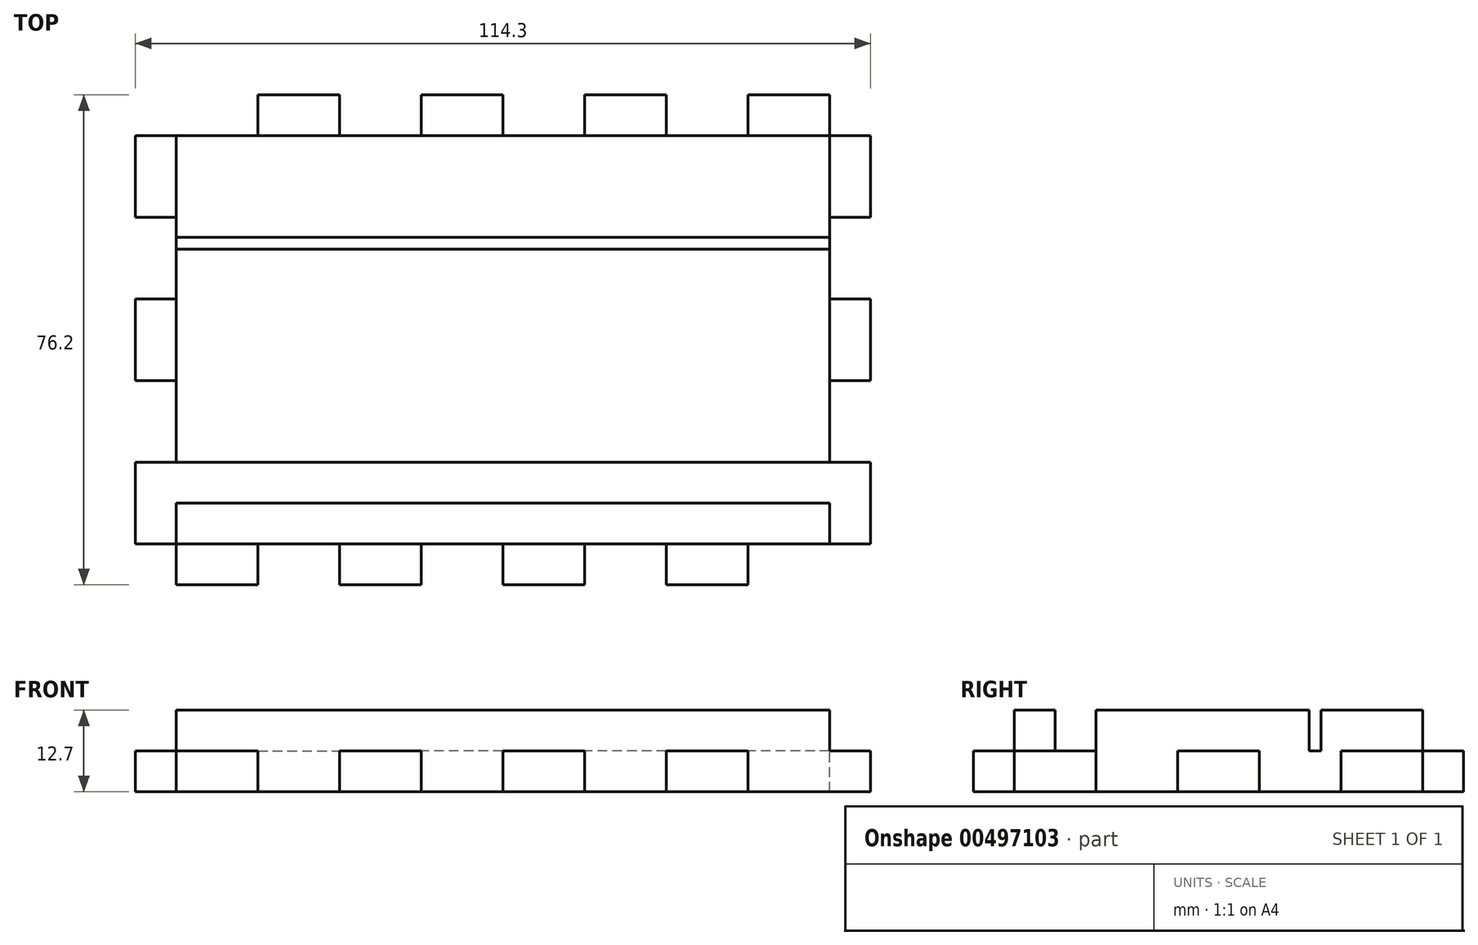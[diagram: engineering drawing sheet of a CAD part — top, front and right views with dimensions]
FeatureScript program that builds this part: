
annotation { "Feature Type Name" : "Feature", "Feature Type Description" : "" }
export const myFeature = defineFeature(function(context is Context, id is Id, definition is map)
    precondition{}
    {
        {
            var Q0;
            Q0=qCreatedBy(makeId("Top.planeOp"),FACE);
            var sketch = newSketch(context, id + "F0", { "sketchPlane" : qUnion([Q0])});
            skLineSegment(sketch, "E0.bottom", {"start": v(50.8, 31.75) * mm, "end": v(-50.8, 31.75) * mm});
            skLineSegment(sketch, "E0.top", {"start": v(50.8, -31.75) * mm, "end": v(-50.8, -31.75) * mm});
            skLineSegment(sketch, "E0.left", {"start": v(50.8, 31.75) * mm, "end": v(50.8, -31.75) * mm});
            skLineSegment(sketch, "E0.right", {"start": v(-50.8, 31.75) * mm, "end": v(-50.8, -31.75) * mm});
            skPoint(sketch, "E0.middle", {"position": v(0, 0) * mm});
            skSolve(sketch);
        }
        {
            var Q0;
            Q0=makeQuery(id+"F0.imprint","IMPRINT",FACE,{"disambiguationData":[TD([[makeQuery(id+"F0.imprint","IMPRINT",EDGE,{"derivedFrom":sQuery(id+"F0.wireOp",EDGE,"E0.bottom")}),1.0]])]});
            extrude(context, id + "F1", {"entities" : qUnion([Q0]), "depth" : 6.35 * mm});
        }
        {
            var Q0;
            Q0=makeQuery(id+"F1.opExtrude","CAP_FACE",FACE,{"disambiguationData":[OSD([sQuery(id+"F0.wireOp",EDGE,"E0.bottom"),sQuery(id+"F0.wireOp",EDGE,"E0.top"),sQuery(id+"F0.wireOp",EDGE,"E0.left"),sQuery(id+"F0.wireOp",EDGE,"E0.right")])],"isStart":false});
            var sketch = newSketch(context, id + "F2", { "sketchPlane" : qUnion([Q0])});
            skLineSegment(sketch, "E1.bottom", {"start": v(50.8, -31.75) * mm, "end": v(-50.8, -31.75) * mm});
            skLineSegment(sketch, "E1.top", {"start": v(50.8, -25.4) * mm, "end": v(-50.8, -25.4) * mm});
            skLineSegment(sketch, "E1.left", {"start": v(50.8, -31.75) * mm, "end": v(50.8, -25.4) * mm});
            skLineSegment(sketch, "E1.right", {"start": v(-50.8, -31.75) * mm, "end": v(-50.8, -25.4) * mm});
            skSolve(sketch);
        }
        {
            var Q0;
            Q0=makeQuery(id+"F2.imprint","IMPRINT",FACE,{"disambiguationData":[TD([[makeQuery(id+"F2.imprint","IMPRINT",EDGE,{"derivedFrom":sQuery(id+"F2.wireOp",EDGE,"E1.bottom")}),-1.0]])]});
            extrude(context, id + "F3", {"entities" : qUnion([Q0]), "operationType" : NewBodyOperationType.ADD, "depth" : 6.35 * mm});
        }
        {
            var Q0;
            Q0=makeQuery(id+"F1.opExtrude","CAP_FACE",FACE,{"disambiguationData":[OSD([sQuery(id+"F0.wireOp",EDGE,"E0.bottom"),sQuery(id+"F0.wireOp",EDGE,"E0.top"),sQuery(id+"F0.wireOp",EDGE,"E0.left"),sQuery(id+"F0.wireOp",EDGE,"E0.right")])],"isStart":false});
            var sketch = newSketch(context, id + "F4", { "sketchPlane" : qUnion([Q0])});
            skLineSegment(sketch, "E2", {"start": v(50.8, -25.4) * mm, "end": v(50.8, -6.22) * mm});
            skLineSegment(sketch, "E3.bottom", {"start": v(50.8, -6.22) * mm, "end": v(-50.8, -6.22) * mm});
            skLineSegment(sketch, "E3.top", {"start": v(50.8, 14.1) * mm, "end": v(-50.8, 14.1) * mm});
            skLineSegment(sketch, "E3.left", {"start": v(50.8, -6.22) * mm, "end": v(50.8, 14.1) * mm});
            skLineSegment(sketch, "E3.right", {"start": v(-50.8, -6.22) * mm, "end": v(-50.8, 14.1) * mm});
            skSolve(sketch);
        }
        {
            var Q0;
            Q0=makeQuery(id+"F4.imprint","IMPRINT",FACE,{"disambiguationData":[TD([[makeQuery(id+"F4.imprint","IMPRINT",EDGE,{"derivedFrom":sQuery(id+"F4.wireOp",EDGE,"E3.bottom")}),-1.0]])]});
            extrude(context, id + "F5", {"entities" : qUnion([Q0]), "operationType" : NewBodyOperationType.ADD, "depth" : 6.35 * mm});
        }
        {
            var Q0;
            {var subQ0=sQuery(id+"F0.wireOp",EDGE,"E0.right");var subQ1=sQuery(id+"F0.wireOp",EDGE,"E0.left");var subQ2=sQuery(id+"F0.wireOp",EDGE,"E0.bottom");Q0=makeQuery(id+"F5.boolean.opBoolean","SPLIT",FACE,{"disambiguationData":[TD([makeQuery(id+"F1.opExtrude","SWEPT_FACE",FACE,{"disambiguationData":[OSD([subQ2])]})])],"derivedFrom":makeQuery(id+"F1.opExtrude","CAP_FACE",FACE,{"disambiguationData":[OSD([subQ2,sQuery(id+"F0.wireOp",EDGE,"E0.top"),subQ1,subQ0])],"isStart":false})});}
            var sketch = newSketch(context, id + "F6", { "sketchPlane" : qUnion([Q0])});
            skLineSegment(sketch, "E4.bottom", {"start": v(-50.8, 14.1) * mm, "end": v(50.8, 14.1) * mm});
            skLineSegment(sketch, "E4.top", {"start": v(-50.8, 22.92) * mm, "end": v(50.8, 22.92) * mm});
            skLineSegment(sketch, "E4.left", {"start": v(-50.8, 14.1) * mm, "end": v(-50.8, 22.92) * mm});
            skLineSegment(sketch, "E4.right", {"start": v(50.8, 14.1) * mm, "end": v(50.8, 22.92) * mm});
            skSolve(sketch);
        }
        {
            var Q0;
            {var subQ0=sQuery(id+"F6.wireOp",EDGE,"E4.top");Q0=makeQuery(id+"F6.imprint","IMPRINT",FACE,{"disambiguationData":[TD([[makeQuery(id+"F6.imprint","IMPRINT",EDGE,{"derivedFrom":subQ0}),1.0]])]});}
            extrude(context, id + "F7", {"entities" : qUnion([Q0]), "operationType" : NewBodyOperationType.ADD, "depth" : 6.35 * mm});
        }
        {
            var Q0;
            Q0=makeQuery(id+"F3.boolean.opBoolean","MERGE",FACE,{"derivedFrom":[makeQuery(id+"F1.opExtrude","SWEPT_FACE",FACE,{"disambiguationData":[OSD([sQuery(id+"F0.wireOp",EDGE,"E0.top")])]}),makeQuery(id+"F3.opExtrude","SWEPT_FACE",FACE,{"disambiguationData":[OSD([sQuery(id+"F2.wireOp",EDGE,"E1.bottom")])]})]});
            var sketch = newSketch(context, id + "F8", { "sketchPlane" : qUnion([Q0])});
            skLineSegment(sketch, "E5.bottom", {"start": v(-50.8, 0) * mm, "end": v(-38.1, 0) * mm});
            skLineSegment(sketch, "E5.top", {"start": v(-50.8, 6.35) * mm, "end": v(-38.1, 6.35) * mm});
            skLineSegment(sketch, "E5.left", {"start": v(-50.8, 0) * mm, "end": v(-50.8, 6.35) * mm});
            skLineSegment(sketch, "E5.right", {"start": v(-38.1, 0) * mm, "end": v(-38.1, 6.35) * mm});
            skLineSegment(sketch, "E6.bottom", {"start": v(-25.4, 0) * mm, "end": v(-12.7, 0) * mm});
            skLineSegment(sketch, "E6.top", {"start": v(-25.4, 6.35) * mm, "end": v(-12.7, 6.35) * mm});
            skLineSegment(sketch, "E6.left", {"start": v(-25.4, 0) * mm, "end": v(-25.4, 6.35) * mm});
            skLineSegment(sketch, "E6.right", {"start": v(-12.7, 0) * mm, "end": v(-12.7, 6.35) * mm});
            skLineSegment(sketch, "E7", {"start": v(-12.7, 0) * mm, "end": v(0, 0) * mm});
            skLineSegment(sketch, "E8.bottom", {"start": v(0, 0) * mm, "end": v(12.7, 0) * mm});
            skLineSegment(sketch, "E8.top", {"start": v(0, 6.35) * mm, "end": v(12.7, 6.35) * mm});
            skLineSegment(sketch, "E8.left", {"start": v(0, 0) * mm, "end": v(0, 6.35) * mm});
            skLineSegment(sketch, "E8.right", {"start": v(12.7, 0) * mm, "end": v(12.7, 6.35) * mm});
            skLineSegment(sketch, "E9.bottom", {"start": v(25.4, 0) * mm, "end": v(38.1, 0) * mm});
            skLineSegment(sketch, "E9.top", {"start": v(25.4, 6.35) * mm, "end": v(38.1, 6.35) * mm});
            skLineSegment(sketch, "E9.left", {"start": v(25.4, 0) * mm, "end": v(25.4, 6.35) * mm});
            skLineSegment(sketch, "E9.right", {"start": v(38.1, 0) * mm, "end": v(38.1, 6.35) * mm});
            skSolve(sketch);
        }
        {
            var Q0;
            Q0=makeQuery(id+"F8.imprint","IMPRINT",FACE,{"disambiguationData":[TD([[makeQuery(id+"F8.imprint","IMPRINT",EDGE,{"derivedFrom":sQuery(id+"F8.wireOp",EDGE,"E5.bottom")}),-1.0]])]});
            var Q1;
            Q1=makeQuery(id+"F8.imprint","IMPRINT",FACE,{"disambiguationData":[TD([[makeQuery(id+"F8.imprint","IMPRINT",EDGE,{"derivedFrom":sQuery(id+"F8.wireOp",EDGE,"E6.bottom")}),-1.0]])]});
            var Q2;
            Q2=makeQuery(id+"F8.imprint","IMPRINT",FACE,{"disambiguationData":[TD([[makeQuery(id+"F8.imprint","IMPRINT",EDGE,{"derivedFrom":sQuery(id+"F8.wireOp",EDGE,"E8.bottom")}),-1.0]])]});
            var Q3;
            Q3=makeQuery(id+"F8.imprint","IMPRINT",FACE,{"disambiguationData":[TD([[makeQuery(id+"F8.imprint","IMPRINT",EDGE,{"derivedFrom":sQuery(id+"F8.wireOp",EDGE,"E9.bottom")}),-1.0]])]});
            extrude(context, id + "F9", {"entities" : qUnion([Q0, Q1, Q2, Q3]), "operationType" : NewBodyOperationType.ADD, "depth" : 6.35 * mm});
        }
        {
            var Q0;
            {var subQ0=sQuery(id+"F0.wireOp",EDGE,"E0.bottom");Q0=makeQuery(id+"F7.boolean.opBoolean","MERGE",FACE,{"derivedFrom":[makeQuery(id+"F1.opExtrude","SWEPT_FACE",FACE,{"disambiguationData":[OSD([subQ0])]}),makeQuery(id+"F7.opExtrude","SWEPT_FACE",FACE,{"disambiguationData":[OSD([subQ0])]})]});}
            var sketch = newSketch(context, id + "F10", { "sketchPlane" : qUnion([Q0])});
            skLineSegment(sketch, "E10", {"start": v(38.1, 6.35) * mm, "end": v(25.4, 6.35) * mm});
            skLineSegment(sketch, "E11.bottom", {"start": v(-50.8, 0) * mm, "end": v(-38.1, 0) * mm});
            skLineSegment(sketch, "E11.top", {"start": v(-50.8, 6.35) * mm, "end": v(-38.1, 6.35) * mm});
            skLineSegment(sketch, "E11.left", {"start": v(-50.8, 0) * mm, "end": v(-50.8, 6.35) * mm});
            skLineSegment(sketch, "E11.right", {"start": v(-38.1, 0) * mm, "end": v(-38.1, 6.35) * mm});
            skLineSegment(sketch, "E12.bottom", {"start": v(-25.4, 0) * mm, "end": v(-12.7, 0) * mm});
            skLineSegment(sketch, "E12.top", {"start": v(-25.4, 6.35) * mm, "end": v(-12.7, 6.35) * mm});
            skLineSegment(sketch, "E12.left", {"start": v(-25.4, 0) * mm, "end": v(-25.4, 6.35) * mm});
            skLineSegment(sketch, "E12.right", {"start": v(-12.7, 0) * mm, "end": v(-12.7, 6.35) * mm});
            skLineSegment(sketch, "E13.bottom", {"start": v(0, 0) * mm, "end": v(12.7, 0) * mm});
            skLineSegment(sketch, "E13.top", {"start": v(0, 6.35) * mm, "end": v(12.7, 6.35) * mm});
            skLineSegment(sketch, "E13.left", {"start": v(0, 0) * mm, "end": v(0, 6.35) * mm});
            skLineSegment(sketch, "E13.right", {"start": v(12.7, 0) * mm, "end": v(12.7, 6.35) * mm});
            skLineSegment(sketch, "E14.bottom", {"start": v(25.4, 0) * mm, "end": v(38.1, 0) * mm});
            skLineSegment(sketch, "E14.top", {"start": v(25.4, 6.35) * mm, "end": v(38.1, 6.35) * mm});
            skLineSegment(sketch, "E14.left", {"start": v(25.4, 0) * mm, "end": v(25.4, 6.35) * mm});
            skLineSegment(sketch, "E14.right", {"start": v(38.1, 0) * mm, "end": v(38.1, 6.35) * mm});
            skLineSegment(sketch, "E15.trimOffspring", {"start": v(12.7, 6.35) * mm, "end": v(0, 6.35) * mm});
            skPoint(sketch, "E16.orphan", {"position": v(50.8, 6.35) * mm});
            skLineSegment(sketch, "E17.trimOffspring", {"start": v(-12.7, 6.35) * mm, "end": v(-25.4, 6.35) * mm});
            skLineSegment(sketch, "E18.trimOffspring", {"start": v(-38.1, 6.35) * mm, "end": v(-50.8, 6.35) * mm});
            skSolve(sketch);
        }
        {
            var Q0;
            Q0=makeQuery(id+"F10.imprint","IMPRINT",FACE,{"disambiguationData":[TD([[makeQuery(id+"F10.imprint","IMPRINT",EDGE,{"derivedFrom":sQuery(id+"F10.wireOp",EDGE,"E11.bottom")}),1.0]])]});
            var Q1;
            Q1=makeQuery(id+"F10.imprint","IMPRINT",FACE,{"disambiguationData":[TD([[makeQuery(id+"F10.imprint","IMPRINT",EDGE,{"derivedFrom":sQuery(id+"F10.wireOp",EDGE,"E12.bottom")}),1.0]])]});
            var Q2;
            Q2=makeQuery(id+"F10.imprint","IMPRINT",FACE,{"disambiguationData":[TD([[makeQuery(id+"F10.imprint","IMPRINT",EDGE,{"derivedFrom":sQuery(id+"F10.wireOp",EDGE,"E13.bottom")}),1.0]])]});
            var Q3;
            Q3=makeQuery(id+"F10.imprint","IMPRINT",FACE,{"disambiguationData":[TD([[makeQuery(id+"F10.imprint","IMPRINT",EDGE,{"derivedFrom":sQuery(id+"F10.wireOp",EDGE,"E14.bottom")}),1.0]])]});
            extrude(context, id + "F11", {"entities" : qUnion([Q0, Q1, Q2, Q3]), "operationType" : NewBodyOperationType.ADD, "depth" : 6.35 * mm});
        }
        {
            var Q0;
            {var subQ0=sQuery(id+"F0.wireOp",EDGE,"E0.right");var subQ1=sQuery(id+"F0.wireOp",EDGE,"E0.left");var subQ2=sQuery(id+"F0.wireOp",EDGE,"E0.bottom");Q0=makeQuery(id+"F5.boolean.opBoolean","SPLIT",FACE,{"disambiguationData":[TD([makeQuery(id+"F1.opExtrude","SWEPT_FACE",FACE,{"disambiguationData":[OSD([subQ2])]})])],"derivedFrom":makeQuery(id+"F1.opExtrude","CAP_FACE",FACE,{"disambiguationData":[OSD([subQ2,sQuery(id+"F0.wireOp",EDGE,"E0.top"),subQ1,subQ0])],"isStart":false})});}
            var sketch = newSketch(context, id + "F12", { "sketchPlane" : qUnion([Q0])});
            skLineSegment(sketch, "E19.bottom", {"start": v(50.8, 14.1) * mm, "end": v(-50.8, 14.1) * mm});
            skLineSegment(sketch, "E19.top", {"start": v(50.8, 15.93) * mm, "end": v(-50.8, 15.93) * mm});
            skLineSegment(sketch, "E19.left", {"start": v(50.8, 14.1) * mm, "end": v(50.8, 15.93) * mm});
            skLineSegment(sketch, "E19.right", {"start": v(-50.8, 14.1) * mm, "end": v(-50.8, 15.93) * mm});
            skSolve(sketch);
        }
        {
            var Q0;
            {var subQ0=sQuery(id+"F12.wireOp",EDGE,"E19.top");Q0=makeQuery(id+"F12.imprint","IMPRINT",FACE,{"disambiguationData":[TD([[makeQuery(id+"F12.imprint","IMPRINT",EDGE,{"derivedFrom":subQ0}),-1.0]])]});}
            extrude(context, id + "F13", {"entities" : qUnion([Q0]), "operationType" : NewBodyOperationType.ADD, "depth" : 6.35 * mm});
        }
        {
            var Q0;
            {var subQ0=sQuery(id+"F0.wireOp",EDGE,"E0.left");Q0=makeQuery(id+"F13.boolean.opBoolean","MERGE",FACE,{"derivedFrom":[makeQuery(id+"F11.boolean.opBoolean","MERGE",FACE,{"derivedFrom":[makeQuery(id+"F7.boolean.opBoolean","MERGE",FACE,{"derivedFrom":[makeQuery(id+"F5.boolean.opBoolean","MERGE",FACE,{"derivedFrom":[makeQuery(id+"F3.boolean.opBoolean","MERGE",FACE,{"derivedFrom":[makeQuery(id+"F1.opExtrude","SWEPT_FACE",FACE,{"disambiguationData":[OSD([subQ0])]}),makeQuery(id+"F3.opExtrude","SWEPT_FACE",FACE,{"disambiguationData":[OSD([sQuery(id+"F2.wireOp",EDGE,"E1.left")])]})]}),makeQuery(id+"F5.opExtrude","SWEPT_FACE",FACE,{"disambiguationData":[OSD([sQuery(id+"F4.wireOp",EDGE,"E3.left")])]})]}),makeQuery(id+"F7.opExtrude","SWEPT_FACE",FACE,{"disambiguationData":[OSD([subQ0])]})]}),makeQuery(id+"F11.opExtrude","SWEPT_FACE",FACE,{"disambiguationData":[OSD([sQuery(id+"F10.wireOp",EDGE,"E11.left")])]})]}),makeQuery(id+"F13.opExtrude","SWEPT_FACE",FACE,{"disambiguationData":[OSD([subQ0])]})]});}
            var sketch = newSketch(context, id + "F14", { "sketchPlane" : qUnion([Q0])});
            skLineSegment(sketch, "E20", {"start": v(0, 6.35) * mm, "end": v(6.35, 6.35) * mm});
            skPoint(sketch, "E20.startSnap0", {"position": v(-15.81, 6.35) * mm});
            skLineSegment(sketch, "E21", {"start": v(0, 6.35) * mm, "end": v(-6.35, 6.35) * mm});
            skLineSegment(sketch, "E22.bottom", {"start": v(6.35, 0) * mm, "end": v(-6.35, 0) * mm});
            skLineSegment(sketch, "E22.top", {"start": v(6.35, 6.35) * mm, "end": v(-6.35, 6.35) * mm});
            skLineSegment(sketch, "E22.left", {"start": v(6.35, 0) * mm, "end": v(6.35, 6.35) * mm});
            skLineSegment(sketch, "E22.right", {"start": v(-6.35, 0) * mm, "end": v(-6.35, 6.35) * mm});
            skPoint(sketch, "E22.middle", {"position": v(0, 3.18) * mm});
            skLineSegment(sketch, "E23.bottom", {"start": v(19.05, 0) * mm, "end": v(31.75, 0) * mm});
            skLineSegment(sketch, "E23.top", {"start": v(19.05, 6.35) * mm, "end": v(31.75, 6.35) * mm});
            skLineSegment(sketch, "E23.left", {"start": v(19.05, 0) * mm, "end": v(19.05, 6.35) * mm});
            skLineSegment(sketch, "E23.right", {"start": v(31.75, 0) * mm, "end": v(31.75, 6.35) * mm});
            skLineSegment(sketch, "E24.bottom", {"start": v(-19.05, 0) * mm, "end": v(-31.75, 0) * mm});
            skLineSegment(sketch, "E24.top", {"start": v(-19.05, 6.35) * mm, "end": v(-31.75, 6.35) * mm});
            skLineSegment(sketch, "E24.left", {"start": v(-19.05, 0) * mm, "end": v(-19.05, 6.35) * mm});
            skLineSegment(sketch, "E24.right", {"start": v(-31.75, 0) * mm, "end": v(-31.75, 6.35) * mm});
            skPoint(sketch, "E25.orphan", {"position": v(0, 0) * mm});
            skSolve(sketch);
        }
        {
            var Q0;
            Q0=makeQuery(id+"F14.imprint","IMPRINT",FACE,{"disambiguationData":[TD([[makeQuery(id+"F14.imprint","IMPRINT",EDGE,{"derivedFrom":sQuery(id+"F14.wireOp",EDGE,"E24.bottom")}),-1.0]])]});
            var Q1;
            Q1=makeQuery(id+"F14.imprint","IMPRINT",FACE,{"disambiguationData":[TD([[makeQuery(id+"F14.imprint","IMPRINT",EDGE,{"derivedFrom":sQuery(id+"F14.wireOp",EDGE,"E22.bottom")}),-1.0]])]});
            var Q2;
            Q2=makeQuery(id+"F14.imprint","IMPRINT",FACE,{"disambiguationData":[TD([[makeQuery(id+"F14.imprint","IMPRINT",EDGE,{"derivedFrom":sQuery(id+"F14.wireOp",EDGE,"E23.bottom")}),-1.0]])]});
            extrude(context, id + "F15", {"entities" : qUnion([Q0, Q1, Q2]), "operationType" : NewBodyOperationType.ADD, "depth" : 6.35 * mm});
        }
        {
            var Q0;
            {var subQ0=sQuery(id+"F0.wireOp",EDGE,"E0.right");Q0=makeQuery(id+"F13.boolean.opBoolean","MERGE",FACE,{"derivedFrom":[makeQuery(id+"F9.boolean.opBoolean","MERGE",FACE,{"derivedFrom":[makeQuery(id+"F7.boolean.opBoolean","MERGE",FACE,{"derivedFrom":[makeQuery(id+"F5.boolean.opBoolean","MERGE",FACE,{"derivedFrom":[makeQuery(id+"F3.boolean.opBoolean","MERGE",FACE,{"derivedFrom":[makeQuery(id+"F1.opExtrude","SWEPT_FACE",FACE,{"disambiguationData":[OSD([subQ0])]}),makeQuery(id+"F3.opExtrude","SWEPT_FACE",FACE,{"disambiguationData":[OSD([sQuery(id+"F2.wireOp",EDGE,"E1.right")])]})]}),makeQuery(id+"F5.opExtrude","SWEPT_FACE",FACE,{"disambiguationData":[OSD([sQuery(id+"F4.wireOp",EDGE,"E3.right")])]})]}),makeQuery(id+"F7.opExtrude","SWEPT_FACE",FACE,{"disambiguationData":[OSD([subQ0])]})]}),makeQuery(id+"F9.opExtrude","SWEPT_FACE",FACE,{"disambiguationData":[OSD([sQuery(id+"F8.wireOp",EDGE,"E5.left")])]})]}),makeQuery(id+"F13.opExtrude","SWEPT_FACE",FACE,{"disambiguationData":[OSD([subQ0])]})]});}
            var sketch = newSketch(context, id + "F16", { "sketchPlane" : qUnion([Q0])});
            skLineSegment(sketch, "E26", {"start": v(0, 6.35) * mm, "end": v(-6.35, 6.35) * mm});
            skLineSegment(sketch, "E27", {"start": v(-31.75, 6.35) * mm, "end": v(-19.05, 6.35) * mm});
            skLineSegment(sketch, "E28", {"start": v(0, 6.35) * mm, "end": v(6.35, 6.35) * mm});
            skLineSegment(sketch, "E29.bottom", {"start": v(-6.35, 0) * mm, "end": v(6.35, 0) * mm});
            skLineSegment(sketch, "E29.top", {"start": v(-6.35, 6.35) * mm, "end": v(6.35, 6.35) * mm});
            skLineSegment(sketch, "E29.left", {"start": v(-6.35, 0) * mm, "end": v(-6.35, 6.35) * mm});
            skLineSegment(sketch, "E29.right", {"start": v(6.35, 0) * mm, "end": v(6.35, 6.35) * mm});
            skPoint(sketch, "E29.middle", {"position": v(0, 3.18) * mm});
            skLineSegment(sketch, "E30.bottom", {"start": v(-19.05, 0) * mm, "end": v(-31.75, 0) * mm});
            skLineSegment(sketch, "E30.top", {"start": v(-19.05, 6.35) * mm, "end": v(-31.75, 6.35) * mm});
            skLineSegment(sketch, "E30.left", {"start": v(-19.05, 0) * mm, "end": v(-19.05, 6.35) * mm});
            skLineSegment(sketch, "E30.right", {"start": v(-31.75, 0) * mm, "end": v(-31.75, 6.35) * mm});
            skLineSegment(sketch, "E31.bottom", {"start": v(19.05, 0) * mm, "end": v(31.75, 0) * mm});
            skLineSegment(sketch, "E31.top", {"start": v(19.05, 6.35) * mm, "end": v(31.75, 6.35) * mm});
            skLineSegment(sketch, "E31.left", {"start": v(19.05, 0) * mm, "end": v(19.05, 6.35) * mm});
            skLineSegment(sketch, "E31.right", {"start": v(31.75, 0) * mm, "end": v(31.75, 6.35) * mm});
            skPoint(sketch, "E32.start.orphan", {"position": v(0, 0) * mm});
            skLineSegment(sketch, "E33.trimOffspring", {"start": v(-6.35, 6.35) * mm, "end": v(0, 6.35) * mm});
            skSolve(sketch);
        }
        {
            var Q0;
            Q0=makeQuery(id+"F16.imprint","IMPRINT",FACE,{"disambiguationData":[TD([[makeQuery(id+"F16.imprint","IMPRINT",EDGE,{"derivedFrom":sQuery(id+"F16.wireOp",EDGE,"E30.bottom")}),1.0]])]});
            var Q1;
            Q1=makeQuery(id+"F16.imprint","IMPRINT",FACE,{"disambiguationData":[TD([[makeQuery(id+"F16.imprint","IMPRINT",EDGE,{"derivedFrom":sQuery(id+"F16.wireOp",EDGE,"E29.bottom")}),1.0]])]});
            var Q2;
            Q2=makeQuery(id+"F16.imprint","IMPRINT",FACE,{"disambiguationData":[TD([[makeQuery(id+"F16.imprint","IMPRINT",EDGE,{"derivedFrom":sQuery(id+"F16.wireOp",EDGE,"E31.bottom")}),1.0]])]});
            extrude(context, id + "F17", {"entities" : qUnion([Q0, Q1, Q2]), "operationType" : NewBodyOperationType.ADD, "depth" : 6.35 * mm});
        }
        {
            var Q0;
            {var subQ0=sQuery(id+"F0.wireOp",EDGE,"E0.right");var subQ1=sQuery(id+"F0.wireOp",EDGE,"E0.left");Q0=makeQuery(id+"F17.boolean.opBoolean","MERGE",FACE,{"derivedFrom":[makeQuery(id+"F15.boolean.opBoolean","MERGE",FACE,{"derivedFrom":[makeQuery(id+"F5.boolean.opBoolean","SPLIT",FACE,{"disambiguationData":[TD([makeQuery(id+"F3.opExtrude","SWEPT_FACE",FACE,{"disambiguationData":[OSD([sQuery(id+"F2.wireOp",EDGE,"E1.top")])]})])],"derivedFrom":makeQuery(id+"F1.opExtrude","CAP_FACE",FACE,{"disambiguationData":[OSD([sQuery(id+"F0.wireOp",EDGE,"E0.bottom"),sQuery(id+"F0.wireOp",EDGE,"E0.top"),subQ1,subQ0])],"isStart":false})}),makeQuery(id+"F15.opExtrude","SWEPT_FACE",FACE,{"disambiguationData":[OSD([sQuery(id+"F14.wireOp",EDGE,"E22.top")])]}),makeQuery(id+"F15.opExtrude","SWEPT_FACE",FACE,{"disambiguationData":[OSD([sQuery(id+"F14.wireOp",EDGE,"E24.top")])]})]}),makeQuery(id+"F17.opExtrude","SWEPT_FACE",FACE,{"disambiguationData":[OSD([sQuery(id+"F16.wireOp",EDGE,"E29.top"),sQuery(id+"F16.wireOp",EDGE,"E33.trimOffspring")])]}),makeQuery(id+"F17.opExtrude","SWEPT_FACE",FACE,{"disambiguationData":[OSD([sQuery(id+"F16.wireOp",EDGE,"E31.top")])]})]});}
            var sketch = newSketch(context, id + "F18", { "sketchPlane" : qUnion([Q0])});
            skLineSegment(sketch, "E34.bottom", {"start": v(-50.8, -6.22) * mm, "end": v(50.8, -6.22) * mm});
            skLineSegment(sketch, "E34.top", {"start": v(-50.8, -19.05) * mm, "end": v(50.8, -19.05) * mm});
            skLineSegment(sketch, "E34.left", {"start": v(-50.8, -6.22) * mm, "end": v(-50.8, -19.05) * mm});
            skLineSegment(sketch, "E34.right", {"start": v(50.8, -6.22) * mm, "end": v(50.8, -19.05) * mm});
            skLineSegment(sketch, "E35", {"start": v(50.8, -6.22) * mm, "end": v(50.8, 6.35) * mm});
            skLineSegment(sketch, "E36", {"start": v(50.8, -19.05) * mm, "end": v(50.8, -31.75) * mm});
            skLineSegment(sketch, "E37", {"start": v(50.8, -19.05) * mm, "end": v(50.8, -6.22) * mm});
            skLineSegment(sketch, "E38", {"start": v(-50.8, -19.05) * mm, "end": v(-50.8, -6.35) * mm});
            skLineSegment(sketch, "E39", {"start": v(-50.8, -6.35) * mm, "end": v(-50.8, 6.35) * mm});
            skLineSegment(sketch, "E40", {"start": v(-50.8, -19.05) * mm, "end": v(-50.8, -31.75) * mm});
            skSolve(sketch);
        }
        {
            var Q0;
            {var subQ5=sQuery(id+"F18.wireOp",EDGE,"E34.bottom");Q0=makeQuery(id+"F18.imprint","IMPRINT",FACE,{"disambiguationData":[TD([[makeQuery(id+"F18.imprint","IMPRINT",EDGE,{"derivedFrom":subQ5}),1.0]])]});}
            extrude(context, id + "F19", {"entities" : qUnion([Q0]), "operationType" : NewBodyOperationType.ADD, "depth" : 6.35 * mm});
        }
    });
